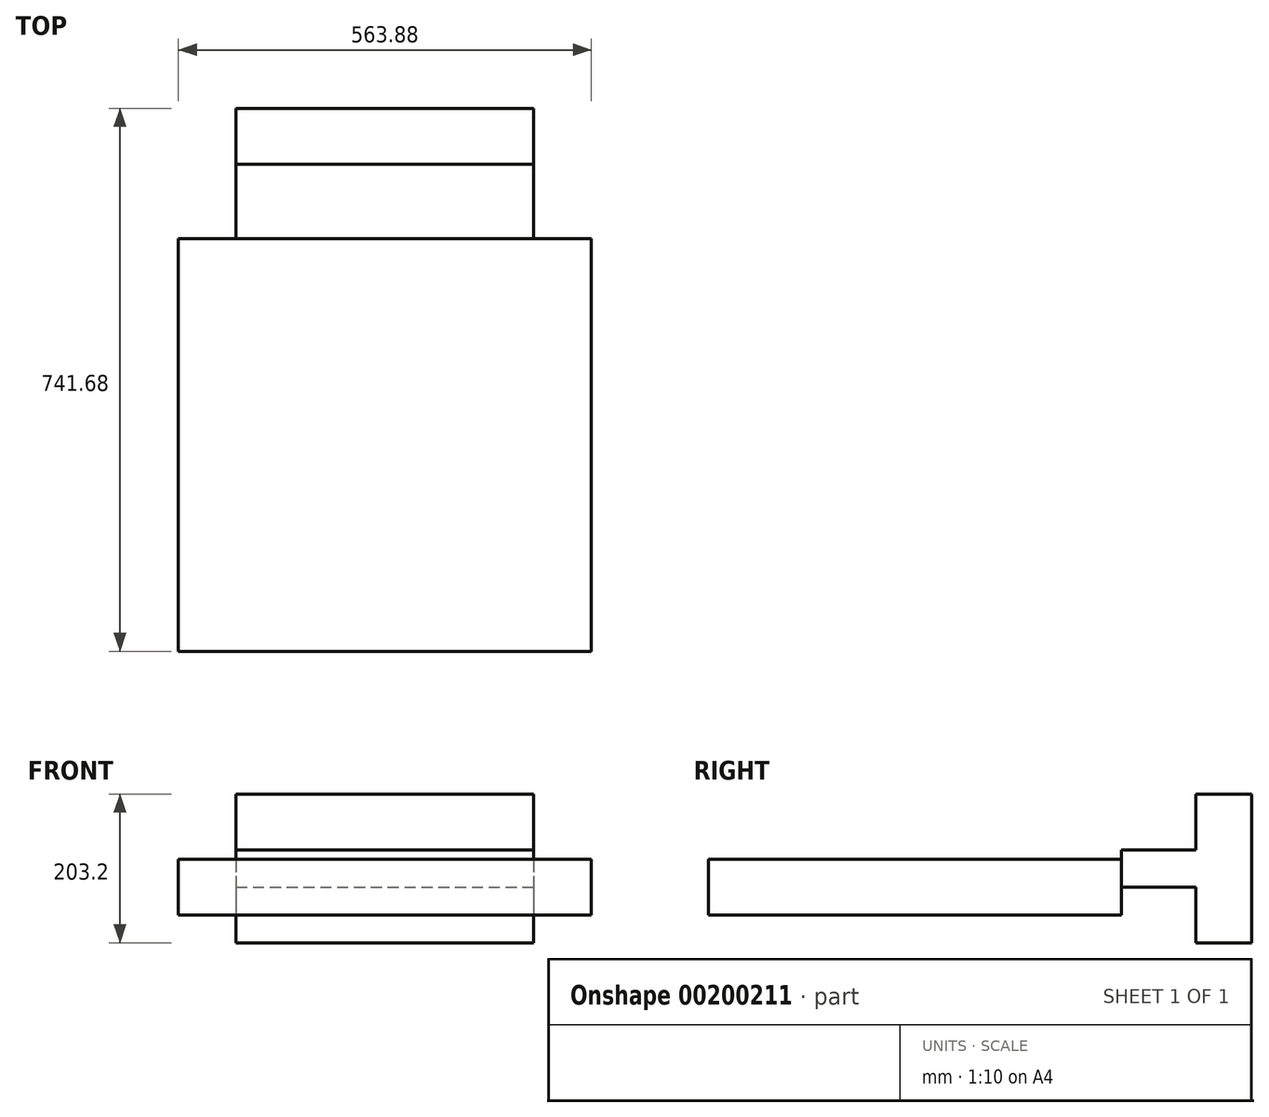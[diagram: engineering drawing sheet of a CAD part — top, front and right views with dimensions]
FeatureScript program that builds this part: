
annotation { "Feature Type Name" : "Feature", "Feature Type Description" : "" }
export const myFeature = defineFeature(function(context is Context, id is Id, definition is map)
    precondition{}
    {
        {
            var Q0;
            Q0=qCreatedBy(makeId("Front.planeOp"),FACE);
            var sketch = newSketch(context, id + "F0", { "sketchPlane" : qUnion([Q0])});
            skLineSegment(sketch, "E0.bottom", {"start": v(-327.38, 116.3) * mm, "end": v(79.02, 116.3) * mm});
            skLineSegment(sketch, "E0.top", {"start": v(-327.38, -86.9) * mm, "end": v(79.02, -86.9) * mm});
            skLineSegment(sketch, "E0.left", {"start": v(-327.38, 116.3) * mm, "end": v(-327.38, -86.9) * mm});
            skLineSegment(sketch, "E0.right", {"start": v(79.02, 116.3) * mm, "end": v(79.02, -86.9) * mm});
            skSolve(sketch);
        }
        {
            var Q0;
            Q0 = qSketchRegion(id + "F0", true);
            extrude(context, id + "F1", {"entities" : qUnion([Q0]), "depth" : 76.2 * mm});
        }
        {
            var Q0;
            Q0=makeQuery(id+"F1.opExtrude","CAP_FACE",FACE,{"disambiguationData":[OSD([sQuery(id+"F0.wireOp",EDGE,"E0.bottom"),sQuery(id+"F0.wireOp",EDGE,"E0.top"),sQuery(id+"F0.wireOp",EDGE,"E0.left"),sQuery(id+"F0.wireOp",EDGE,"E0.right")])],"isStart":false});
            var sketch = newSketch(context, id + "F2", { "sketchPlane" : qUnion([Q0])});
            skLineSegment(sketch, "E1.bottom", {"start": v(-327.38, 40.1) * mm, "end": v(79.02, 40.1) * mm});
            skLineSegment(sketch, "E1.top", {"start": v(-327.38, -10.7) * mm, "end": v(79.02, -10.7) * mm});
            skLineSegment(sketch, "E1.left", {"start": v(-327.38, 40.1) * mm, "end": v(-327.38, -10.7) * mm});
            skLineSegment(sketch, "E1.right", {"start": v(79.02, 40.1) * mm, "end": v(79.02, -10.7) * mm});
            skSolve(sketch);
        }
        {
            var Q0;
            Q0=makeQuery(id+"F2.imprint","IMPRINT",FACE,{"disambiguationData":[TD([[makeQuery(id+"F2.imprint","IMPRINT",EDGE,{"derivedFrom":sQuery(id+"F2.wireOp",EDGE,"E1.bottom")}),-1.0]])]});
            extrude(context, id + "F3", {"entities" : qUnion([Q0]), "operationType" : NewBodyOperationType.ADD, "depth" : 101.6 * mm});
        }
        {
            var Q0;
            Q0=makeQuery(id+"F3.opExtrude","SWEPT_FACE",FACE,{"disambiguationData":[OSD([sQuery(id+"F2.wireOp",EDGE,"E1.top")])]});
            var sketch = newSketch(context, id + "F4", { "sketchPlane" : qUnion([Q0])});
            skLineSegment(sketch, "E2.bottom", {"start": v(-406.12, 177.8) * mm, "end": v(157.76, 177.8) * mm});
            skLineSegment(sketch, "E2.top", {"start": v(-406.12, 741.68) * mm, "end": v(157.76, 741.68) * mm});
            skLineSegment(sketch, "E2.left", {"start": v(-406.12, 177.8) * mm, "end": v(-406.12, 741.68) * mm});
            skLineSegment(sketch, "E2.right", {"start": v(157.76, 177.8) * mm, "end": v(157.76, 741.68) * mm});
            skSolve(sketch);
        }
        {
            var Q0;
            Q0=makeQuery(id+"F4.imprint","IMPRINT",FACE,{"disambiguationData":[TD([[makeQuery(id+"F4.imprint","IMPRINT",EDGE,{"derivedFrom":sQuery(id+"F4.wireOp",EDGE,"E2.top")}),-1.0]])]});
            extrude(context, id + "F5", {"entities" : qUnion([Q0]), "operationType" : NewBodyOperationType.ADD, "endBound" : BoundingType.SYMMETRIC, "depth" : 76.2 * mm});
        }
    });
